FREECAD ASSEMBLY — COMPONENT RECIPES ("testingassembly")

This assembly document has 2 components, labeled P0..P1 below (a component is one placed body or linked part). 0 of them carry a construction recipe — the FreeCAD feature program that regenerates the part from scratch, quoted from this document or its linked companion documents; the rest are supplied as boundary geometry only. No exploded tour is included for this assembly.
COMPONENT P0 — geometry summary ("Part001"; no construction recipe available for this part):
  bounding box: 130.1 x 86.0 x 50.0 mm
  tessellated surface: 7,668 triangles
  volume: 139604 mm^3 (25% of its bounding box)
  symmetry: mirror-symmetric across its x mid-plane
COMPONENT P1 — geometry summary ("Part002"; no construction recipe available for this part):
  bounding box: 65.0 x 20.0 x 20.0 mm
  tessellated surface: 2,214 triangles
  volume: 9733 mm^3 (37% of its bounding box)
  symmetry: mirror-symmetric across its y mid-plane
PROVENANCE & LICENSES
A FreeCAD (.FCStd) document from a public repository crawl; recipes are the document's own serialized feature recipes (and, for linked parts, companion documents' recipes).
License: as declared in the source repository (recorded in the dataset sidecar).
